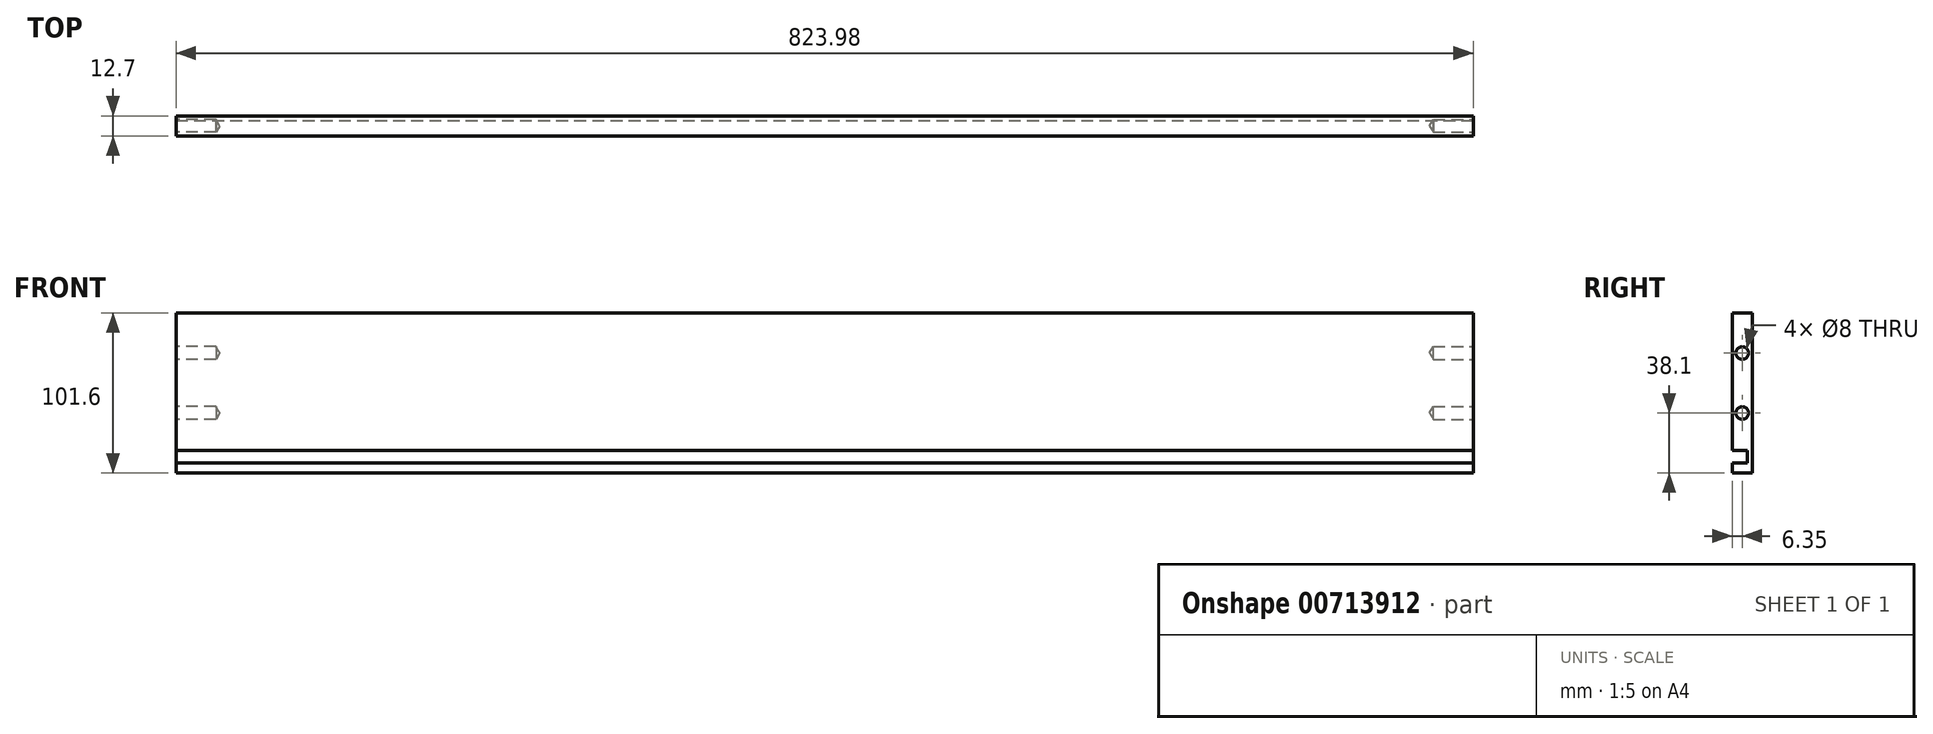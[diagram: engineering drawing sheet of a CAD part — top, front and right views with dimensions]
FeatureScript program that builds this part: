
annotation { "Feature Type Name" : "Feature", "Feature Type Description" : "" }
export const myFeature = defineFeature(function(context is Context, id is Id, definition is map)
    precondition{}
    {
        {
            var Q0;
            Q0=qCreatedBy(makeId("Front.planeOp"),FACE);
            var sketch = newSketch(context, id + "F0", { "sketchPlane" : qUnion([Q0])});
            skLineSegment(sketch, "E0.bottom", {"start": v(411.99, 50.8) * mm, "end": v(-411.99, 50.8) * mm});
            skLineSegment(sketch, "E0.top", {"start": v(411.99, -50.8) * mm, "end": v(-411.99, -50.8) * mm});
            skLineSegment(sketch, "E0.left", {"start": v(411.99, 50.8) * mm, "end": v(411.99, -50.8) * mm});
            skLineSegment(sketch, "E0.right", {"start": v(-411.99, 50.8) * mm, "end": v(-411.99, -50.8) * mm});
            skPoint(sketch, "E0.middle", {"position": v(0, 0) * mm});
            skSolve(sketch);
        }
        {
            var Q0;
            Q0=makeQuery(id+"F0.imprint","IMPRINT",FACE,{"disambiguationData":[TD([[makeQuery(id+"F0.imprint","IMPRINT",EDGE,{"derivedFrom":sQuery(id+"F0.wireOp",EDGE,"E0.bottom")}),1.0]])]});
            extrude(context, id + "F1", {"entities" : qUnion([Q0]), "depth" : 12.7 * mm, "offsetDistance" : 25.4 * mm});
        }
        {
            var Q0;
            Q0=makeQuery(id+"F1.opExtrude","CAP_FACE",FACE,{"disambiguationData":[OSD([sQuery(id+"F0.wireOp",EDGE,"E0.bottom"),sQuery(id+"F0.wireOp",EDGE,"E0.top"),sQuery(id+"F0.wireOp",EDGE,"E0.left"),sQuery(id+"F0.wireOp",EDGE,"E0.right")])],"isStart":false});
            var sketch = newSketch(context, id + "F2", { "sketchPlane" : qUnion([Q0])});
            skLineSegment(sketch, "E1", {"start": v(-411.99, -50.8) * mm, "end": v(-411.99, -44.45) * mm});
            skLineSegment(sketch, "E2.bottom", {"start": v(-411.99, -44.45) * mm, "end": v(411.99, -44.45) * mm});
            skLineSegment(sketch, "E2.top", {"start": v(-411.99, -36.58) * mm, "end": v(411.99, -36.58) * mm});
            skLineSegment(sketch, "E2.left", {"start": v(-411.99, -44.45) * mm, "end": v(-411.99, -36.58) * mm});
            skLineSegment(sketch, "E2.right", {"start": v(411.99, -44.45) * mm, "end": v(411.99, -36.58) * mm});
            skSolve(sketch);
        }
        {
            var Q0;
            Q0=makeQuery(id+"F2.imprint","IMPRINT",FACE,{"disambiguationData":[TD([[makeQuery(id+"F2.imprint","IMPRINT",EDGE,{"derivedFrom":sQuery(id+"F2.wireOp",EDGE,"E2.bottom")}),1.0]])]});
            extrude(context, id + "F3", {"entities" : qUnion([Q0]), "operationType" : NewBodyOperationType.REMOVE, "oppositeDirection" : true, "depth" : 9.65 * mm, "offsetDistance" : 25.4 * mm});
        }
        {
            var Q0;
            Q0=makeQuery(id+"F1.opExtrude","SWEPT_FACE",FACE,{"disambiguationData":[OSD([sQuery(id+"F0.wireOp",EDGE,"E0.right")])]});
            var sketch = newSketch(context, id + "F4", { "sketchPlane" : qUnion([Q0])});
            skLineSegment(sketch, "E3", {"start": v(6.35, 50.8) * mm, "end": v(6.35, 25.4) * mm});
            skLineSegment(sketch, "E4", {"start": v(6.35, 25.4) * mm, "end": v(6.35, -12.7) * mm});
            skPoint(sketch, "E5", {"position": v(6.35, 25.4) * mm});
            skPoint(sketch, "E6", {"position": v(6.35, -12.7) * mm});
            skSolve(sketch);
        }
        {
            var Q0;
            Q0=sQuery(id+"F4.wireOp",VERTEX,"E5");
            var Q1;
            Q1=sQuery(id+"F4.wireOp",VERTEX,"E6");
            var Q2;
            Q2=sQuery(id+"F4.wireOp",VERTEX,"6e459557-0d35-47b1-9956-6053886e1561");
            var Q3;
            Q3=makeQuery(id+"F1.opExtrude","SWEPT_BODY",BODY,{"disambiguationData":[OSD([sQuery(id+"F0.wireOp",EDGE,"E0.bottom"),sQuery(id+"F0.wireOp",EDGE,"E0.top"),sQuery(id+"F0.wireOp",EDGE,"E0.left"),sQuery(id+"F0.wireOp",EDGE,"E0.right")])]});
            hole(context, id + "F5", {"style" : HoleStyle.SIMPLE, "endStyle" : HoleEndStyle.BLIND, "holeDiameter" : 8 * mm, "majorDiameter" : 6.35 * mm, "holeDepth" : 25.4 * mm, "isTappedThrough" : true, "tappedDepth" : 12.7 * mm, "tapClearance" : 3, "startFromSketch" : true, "locations" : qUnion([Q0, Q1, Q2]), "scope" : qUnion([Q3])});
        }
        {
            var Q0;
            Q0=makeQuery(id+"F1.opExtrude","SWEPT_FACE",FACE,{"disambiguationData":[OSD([sQuery(id+"F0.wireOp",EDGE,"E0.left")])]});
            var sketch = newSketch(context, id + "F6", { "sketchPlane" : qUnion([Q0])});
            skLineSegment(sketch, "E7", {"start": v(-6.35, 50.8) * mm, "end": v(-6.35, 25.4) * mm});
            skLineSegment(sketch, "E8", {"start": v(-6.35, 25.4) * mm, "end": v(-6.35, -12.7) * mm});
            skPoint(sketch, "E9", {"position": v(-6.35, 25.4) * mm});
            skPoint(sketch, "E10", {"position": v(-6.35, -12.7) * mm});
            skSolve(sketch);
        }
        {
            var Q0;
            Q0=sQuery(id+"F6.wireOp",VERTEX,"E9");
            var Q1;
            Q1=sQuery(id+"F6.wireOp",VERTEX,"E10");
            var Q2;
            Q2=sQuery(id+"F6.wireOp",VERTEX,"8ebdade1-9f64-4c1d-9ad5-254a5925b829");
            var Q3;
            Q3=makeQuery(id+"F1.opExtrude","SWEPT_BODY",BODY,{"disambiguationData":[OSD([sQuery(id+"F0.wireOp",EDGE,"E0.bottom"),sQuery(id+"F0.wireOp",EDGE,"E0.top"),sQuery(id+"F0.wireOp",EDGE,"E0.left"),sQuery(id+"F0.wireOp",EDGE,"E0.right")])]});
            hole(context, id + "F7", {"style" : HoleStyle.SIMPLE, "endStyle" : HoleEndStyle.BLIND, "holeDiameter" : 8 * mm, "majorDiameter" : 6.35 * mm, "holeDepth" : 25.4 * mm, "isTappedThrough" : true, "tappedDepth" : 12.7 * mm, "tapClearance" : 3, "startFromSketch" : true, "locations" : qUnion([Q0, Q1, Q2]), "scope" : qUnion([Q3])});
        }
    });
